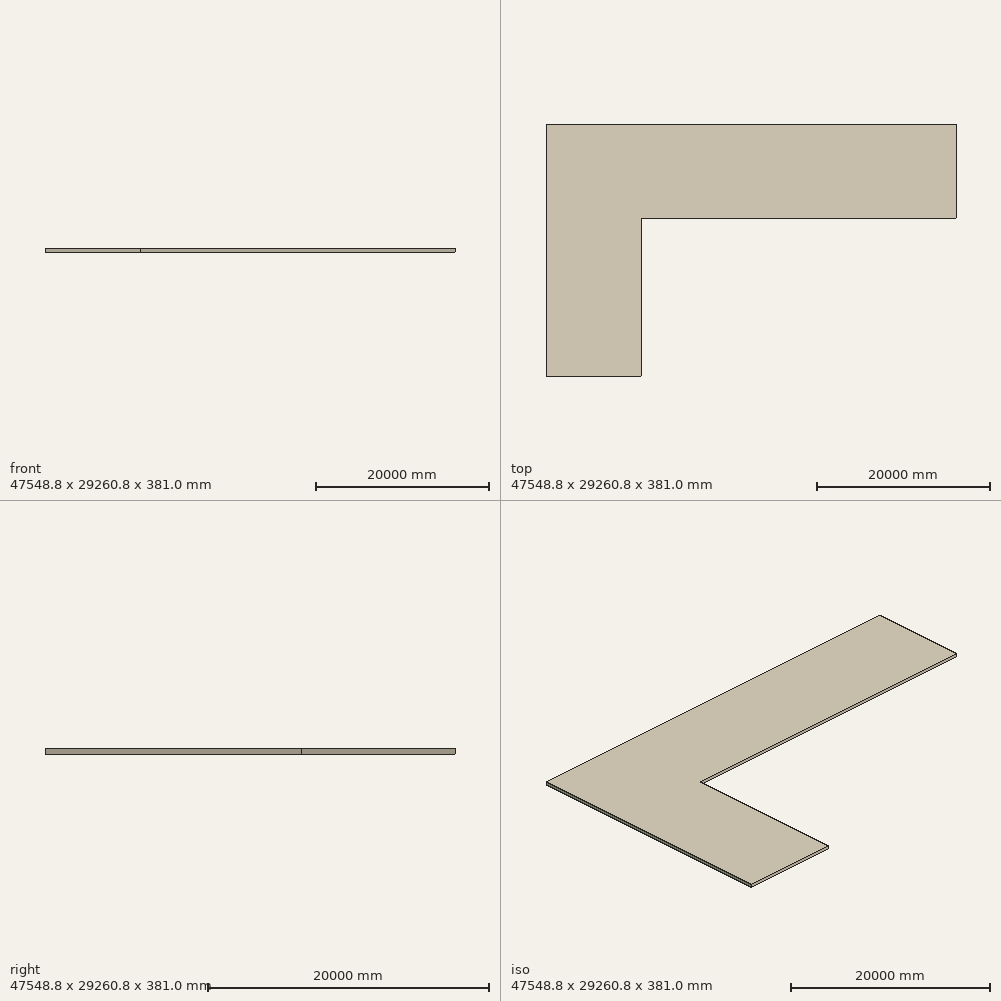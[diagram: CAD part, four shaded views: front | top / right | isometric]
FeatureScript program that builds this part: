
annotation { "Feature Type Name" : "Feature", "Feature Type Description" : "" }
export const myFeature = defineFeature(function(context is Context, id is Id, definition is map)
    precondition{}
    {
        {
            var Q0;
            Q0=qCreatedBy(makeId("Top.planeOp"),FACE);
            cPlane(context, id + "F0", {"entities" : qUnion([Q0]), "cplaneType" : CPlaneType.OFFSET, "offset" : 3048 * mm, "width" : 152.4 * mm, "height" : 152.4 * mm});
        }
        {
            var Q0;
            Q0=qCreatedBy(id+"F0.planeOp",FACE);
            var sketch = newSketch(context, id + "F1", { "sketchPlane" : qUnion([Q0])});
            skLineSegment(sketch, "E0", {"start": v(-914.4, 914.4) * mm, "end": v(46634.4, 914.4) * mm});
            skLineSegment(sketch, "E1", {"start": v(46634.4, 914.4) * mm, "end": v(46634.4, -10058.4) * mm});
            skLineSegment(sketch, "E2", {"start": v(46634.4, -10058.4) * mm, "end": v(10058.4, -10058.4) * mm});
            skLineSegment(sketch, "E3", {"start": v(10058.4, -10058.4) * mm, "end": v(10058.4, -28346.4) * mm});
            skLineSegment(sketch, "E4", {"start": v(10058.4, -28346.4) * mm, "end": v(-914.4, -28346.4) * mm});
            skLineSegment(sketch, "E5", {"start": v(-914.4, -28346.4) * mm, "end": v(-914.4, 914.4) * mm});
            skSolve(sketch);
        }
        {
            var Q0;
            Q0=makeQuery(id+"F1.imprint","IMPRINT",FACE,{"disambiguationData":[TD([[makeQuery(id+"F1.imprint","IMPRINT",EDGE,{"derivedFrom":sQuery(id+"F1.wireOp",EDGE,"E0")}),-1.0]])]});
            extrude(context, id + "F2", {"entities" : qUnion([Q0]), "depth" : 381 * mm, "offsetDistance" : 30.48 * mm});
        }
    });
